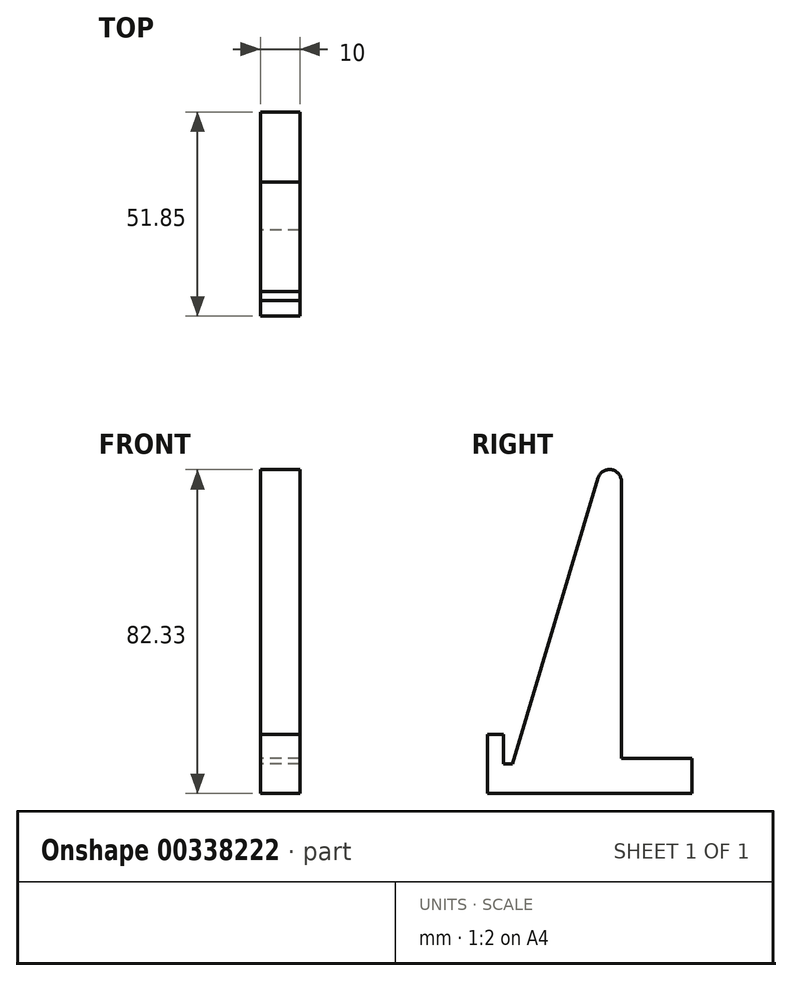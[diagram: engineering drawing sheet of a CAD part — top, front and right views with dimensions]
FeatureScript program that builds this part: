
annotation { "Feature Type Name" : "Feature", "Feature Type Description" : "" }
export const myFeature = defineFeature(function(context is Context, id is Id, definition is map)
    precondition{}
    {
        {
            var Q0;
            Q0=qCreatedBy(makeId("Right.planeOp"),FACE);
            var sketch = newSketch(context, id + "F0", { "sketchPlane" : qUnion([Q0])});
            skLineSegment(sketch, "E0", {"start": v(-44.75, 1.14) * mm, "end": v(-14.75, 101.14) * mm});
            skLineSegment(sketch, "E1", {"start": v(-14.75, 1.14) * mm, "end": v(-44.75, 1.14) * mm});
            skLineSegment(sketch, "E2", {"start": v(-14.75, 1.14) * mm, "end": v(-14.75, 101.14) * mm});
            skLineSegment(sketch, "E3.bottom", {"start": v(-44.74, 16.15) * mm, "end": v(-48.74, 16.15) * mm});
            skLineSegment(sketch, "E3.top", {"start": v(-44.74, 1.15) * mm, "end": v(-48.74, 1.15) * mm});
            skLineSegment(sketch, "E3.left", {"start": v(-44.74, 16.15) * mm, "end": v(-44.74, 1.15) * mm});
            skLineSegment(sketch, "E3.right", {"start": v(-48.74, 16.15) * mm, "end": v(-48.74, 1.15) * mm});
            skLineSegment(sketch, "E4.bottom", {"start": v(-44.74, 8.65) * mm, "end": v(-40.24, 8.65) * mm});
            skLineSegment(sketch, "E4.top", {"start": v(-44.74, 1.15) * mm, "end": v(-40.24, 1.15) * mm});
            skLineSegment(sketch, "E4.left", {"start": v(-44.74, 8.65) * mm, "end": v(-44.74, 1.15) * mm});
            skLineSegment(sketch, "E4.right", {"start": v(-40.24, 8.65) * mm, "end": v(-40.24, 1.15) * mm});
            skLineSegment(sketch, "E5.bottom", {"start": v(-26.89, 10.14) * mm, "end": v(3.11, 10.14) * mm});
            skLineSegment(sketch, "E5.top", {"start": v(-26.89, 1.14) * mm, "end": v(3.11, 1.14) * mm});
            skLineSegment(sketch, "E5.left", {"start": v(-26.89, 10.14) * mm, "end": v(-26.89, 1.14) * mm});
            skLineSegment(sketch, "E5.right", {"start": v(3.11, 10.14) * mm, "end": v(3.11, 1.14) * mm});
            skSolve(sketch);
        }
        {
            var Q0;
            {var subQ4=sQuery(id+"F0.wireOp",EDGE,"E5.top");Q0=makeQuery(id+"F0.imprint","IMPRINT",FACE,{"disambiguationData":[TD([[makeQuery(id+"F0.imprint","IMPRINT",EDGE,{"derivedFrom":subQ4}),1.0]])]});}
            var Q1;
            {var subQ0=sQuery(id+"F0.wireOp",EDGE,"E2");var subQ1=sQuery(id+"F0.wireOp",EDGE,"E1");var subQ2=makeQuery(id+"F0.imprint","INTERSECT",VERTEX,{"derivedFrom":[subQ1,subQ0]});Q1=makeQuery(id+"F0.imprint","IMPRINT",FACE,{"disambiguationData":[TD([[makeQuery(id+"F0.imprint","IMPRINT",EDGE,{"disambiguationData":[TD([[subQ2,-1.0]])],"derivedFrom":subQ1}),-1.0]])]});}
            var Q2;
            {var subQ15=sQuery(id+"F0.wireOp",EDGE,"E4.top");Q2=makeQuery(id+"F0.imprint","IMPRINT",FACE,{"disambiguationData":[TD([[makeQuery(id+"F0.imprint","IMPRINT",EDGE,{"derivedFrom":subQ15}),-1.0]])]});}
            var Q3;
            Q3=makeQuery(id+"F0.imprint","IMPRINT",FACE,{"disambiguationData":[TD([[makeQuery(id+"F0.imprint","IMPRINT",EDGE,{"derivedFrom":sQuery(id+"F0.wireOp",EDGE,"E3.bottom")}),1.0]])]});
            var Q4;
            {var subQ0=sQuery(id+"F0.wireOp",EDGE,"E4.bottom");var subQ1=sQuery(id+"F0.wireOp",EDGE,"E0");var subQ2=makeQuery(id+"F0.imprint","INTERSECT",VERTEX,{"derivedFrom":[subQ1,subQ0]});Q4=makeQuery(id+"F0.imprint","IMPRINT",FACE,{"disambiguationData":[TD([[makeQuery(id+"F0.imprint","IMPRINT",EDGE,{"disambiguationData":[TD([[subQ2,1.0]])],"derivedFrom":subQ1}),1.0]])]});}
            var Q5;
            {var subQ0=sQuery(id+"F0.wireOp",EDGE,"E4.top");Q5=makeQuery(id+"F0.imprint","IMPRINT",FACE,{"disambiguationData":[TD([[makeQuery(id+"F0.imprint","IMPRINT",EDGE,{"derivedFrom":subQ0}),1.0]])]});}
            var Q6;
            {var subQ0=sQuery(id+"F0.wireOp",EDGE,"E3.top");var subQ1=sQuery(id+"F0.wireOp",EDGE,"E0");var subQ2=makeQuery(id+"F0.imprint","INTERSECT",VERTEX,{"derivedFrom":[subQ1,subQ0]});Q6=makeQuery(id+"F0.imprint","IMPRINT",FACE,{"disambiguationData":[TD([[makeQuery(id+"F0.imprint","IMPRINT",EDGE,{"disambiguationData":[TD([[subQ2,-1.0]])],"derivedFrom":subQ1}),-1.0]])]});}
            extrude(context, id + "F1", {"entities" : qUnion([Q0, Q1, Q2, Q3, Q4, Q5, Q6]), "depth" : 10 * mm});
        }
        {
            var Q0;
            Q0=makeQuery(id+"F1.opExtrude","SWEPT_EDGE",EDGE,{"disambiguationData":[OSD([sQuery(id+"F0.wireOp",EDGE,"E0"),sQuery(id+"F0.wireOp",EDGE,"E2")])]});
            fillet(context, id + "F2", {"entities" : qUnion([Q0]), "radius" : 3.04 * mm, "tangentPropagation" : true, "allowEdgeOverflow" : false});
        }
    });
